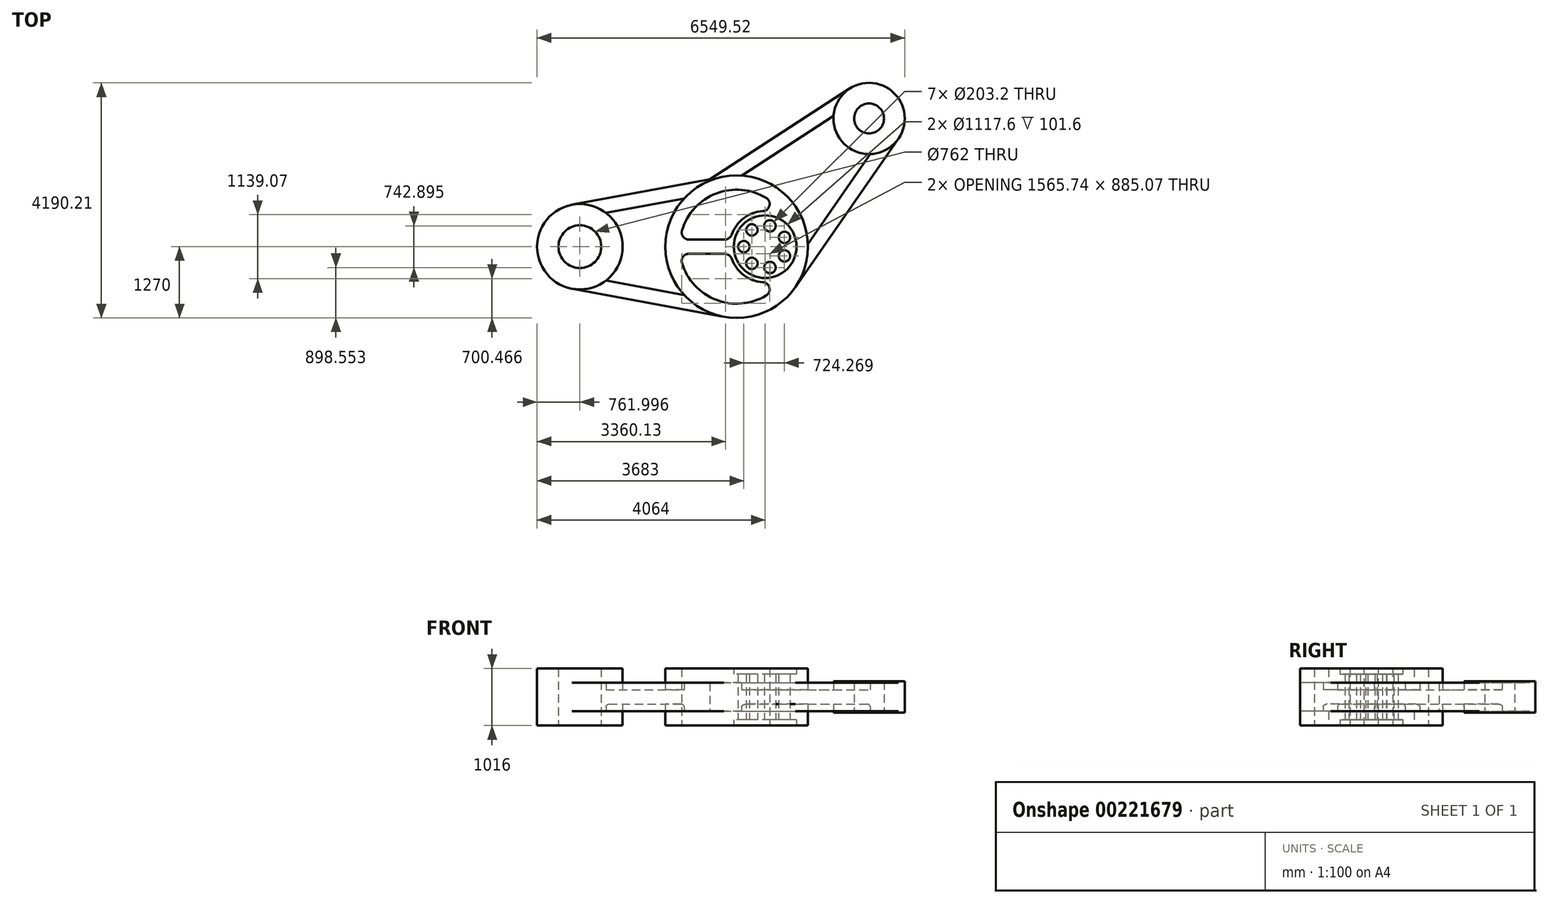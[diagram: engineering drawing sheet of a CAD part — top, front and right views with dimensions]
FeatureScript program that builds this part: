
annotation { "Feature Type Name" : "Feature", "Feature Type Description" : "" }
export const myFeature = defineFeature(function(context is Context, id is Id, definition is map)
    precondition{}
    {
        {
            var Q0;
            Q0=qCreatedBy(makeId("Top.planeOp"),FACE);
            var sketch = newSketch(context, id + "F0", { "sketchPlane" : qUnion([Q0])});
            skCircle(sketch, "E0", {"center": v(-3374.84, 0) * mm, "radius": 762 * mm});
            skCircle(sketch, "E1", {"center": v(-580.84, 0) * mm, "radius": 1270 * mm});
            skCircle(sketch, "E2", {"center": v(1777.68, 2285.21) * mm, "radius": 635 * mm});
            skCircle(sketch, "E3", {"center": v(-3374.84, 0) * mm, "radius": 381 * mm});
            skArc(sketch, "E4", {"start": v(-695.01, -127) * mm, "mid": v(-307.44, -590.07) * mm, "end": v(292.28, -519.53) * mm});
            skCircle(sketch, "E5", {"center": v(1777.68, 2285.21) * mm, "radius": 266.7 * mm});
            skArc(sketch, "E6", {"start": v(-1588.88, -127) * mm, "mid": v(-788.38, -994.58) * mm, "end": v(292.28, -519.53) * mm});
            skCircle(sketch, "E7", {"center": v(-72.84, 0) * mm, "radius": 558.8 * mm});
            skLineSegment(sketch, "E8", {"start": v(-3374.84, 0) * mm, "end": v(689.16, 0) * mm, "construction": true});
            skPoint(sketch, "E9.middle", {"position": v(-499.06, 0) * mm});
            skLineSegment(sketch, "E10", {"start": v(-3513.39, -749.3) * mm, "end": v(-811.75, -1248.83) * mm});
            skLineSegment(sketch, "E11", {"start": v(-3513.39, 749.3) * mm, "end": v(-1059.83, 1202.96) * mm});
            skLineSegment(sketch, "E12", {"start": v(462.58, -724) * mm, "end": v(2299.4, 1923.21) * mm});
            skLineSegment(sketch, "E13", {"start": v(-1059.83, 1202.96) * mm, "end": v(1432.34, 2818.1) * mm});
            skLineSegment(sketch, "E14.0", {"start": v(-2908.71, 602.8) * mm, "end": v(-1514.87, 860.52) * mm});
            skLineSegment(sketch, "E15.0", {"start": v(-2908.71, -602.8) * mm, "end": v(-1514.87, -860.52) * mm});
            skLineSegment(sketch, "E16.0", {"start": v(-493.95, 1267.02) * mm, "end": v(1144.17, 2328.66) * mm});
            skLineSegment(sketch, "E17.trimOffspring", {"start": v(688.3, 46.85) * mm, "end": v(1801.11, 1650.65) * mm});
            skLineSegment(sketch, "E18", {"start": v(-695.01, 127) * mm, "end": v(-1588.88, 127) * mm});
            skLineSegment(sketch, "E19.MirrorCS", {"start": v(-695.01, -127) * mm, "end": v(-1588.88, -127) * mm});
            skArc(sketch, "E20.trimOffspring", {"start": v(292.28, 519.53) * mm, "mid": v(-307.44, 590.07) * mm, "end": v(-695.01, 127) * mm});
            skArc(sketch, "E21.trimOffspring", {"start": v(292.28, 519.53) * mm, "mid": v(-788.38, 994.58) * mm, "end": v(-1588.88, 127) * mm});
            skPoint(sketch, "E22.center", {"position": v(0, 0) * mm});
            skLineSegment(sketch, "E23", {"start": v(-72.84, 0) * mm, "end": v(1777.68, 2285.21) * mm, "construction": true});
            skCircle(sketch, "E24", {"center": v(-453.84, 0) * mm, "radius": 101.6 * mm});
            skCircle(sketch, "E25.1.0", {"center": v(-310.4, -297.88) * mm, "radius": 101.6 * mm});
            skCircle(sketch, "E25.2.0", {"center": v(11.94, -371.45) * mm, "radius": 101.6 * mm});
            skCircle(sketch, "E25.3.0", {"center": v(270.42, -165.3) * mm, "radius": 101.6 * mm});
            skCircle(sketch, "E25.4.0", {"center": v(270.42, 165.3) * mm, "radius": 101.6 * mm});
            skCircle(sketch, "E25.5.0", {"center": v(11.94, 371.45) * mm, "radius": 101.6 * mm});
            skCircle(sketch, "E25.6.0", {"center": v(-310.4, 297.88) * mm, "radius": 101.6 * mm});
            skSolve(sketch);
        }
        {
            var Q0;
            Q0=makeQuery(id+"F0.imprint","IMPRINT",FACE,{"disambiguationData":[TD([[makeQuery(id+"F0.imprint","IMPRINT",EDGE,{"derivedFrom":sQuery(id+"F0.wireOp",EDGE,"E4")}),1.0]])]});
            extrude(context, id + "F1", {"entities" : qUnion([Q0]), "endBound" : BoundingType.SYMMETRIC, "depth" : 1016 * mm});
        }
        {
            var Q0;
            Q0=makeQuery(id+"F0.imprint","IMPRINT",FACE,{"disambiguationData":[TD([[makeQuery(id+"F0.imprint","IMPRINT",EDGE,{"derivedFrom":sQuery(id+"F0.wireOp",EDGE,"E7")}),1.0]])]});
            extrude(context, id + "F2", {"entities" : qUnion([Q0]), "operationType" : NewBodyOperationType.ADD, "endBound" : BoundingType.SYMMETRIC, "depth" : 812.8 * mm});
        }
        {
            var Q0;
            {var subQ3=sQuery(id+"F0.wireOp",EDGE,"E11");Q0=makeQuery(id+"F0.imprint","IMPRINT",FACE,{"disambiguationData":[TD([[makeQuery(id+"F0.imprint","IMPRINT",EDGE,{"derivedFrom":subQ3}),-1.0]])]});}
            extrude(context, id + "F3", {"entities" : qUnion([Q0]), "operationType" : NewBodyOperationType.ADD, "endBound" : BoundingType.SYMMETRIC, "depth" : 508 * mm});
        }
        {
            var Q0;
            {var subQ0=sQuery(id+"F0.wireOp",EDGE,"E10");Q0=makeQuery(id+"F0.imprint","IMPRINT",FACE,{"disambiguationData":[TD([[makeQuery(id+"F0.imprint","IMPRINT",EDGE,{"derivedFrom":subQ0}),1.0]])]});}
            var Q1;
            {var subQ0=sQuery(id+"F0.wireOp",EDGE,"E12");Q1=makeQuery(id+"F0.imprint","IMPRINT",FACE,{"disambiguationData":[TD([[makeQuery(id+"F0.imprint","IMPRINT",EDGE,{"derivedFrom":subQ0}),1.0]])]});}
            extrude(context, id + "F4", {"entities" : qUnion([Q0, Q1]), "operationType" : NewBodyOperationType.ADD, "endBound" : BoundingType.SYMMETRIC, "depth" : 508 * mm});
        }
        {
            var Q0;
            {var subQ0=sQuery(id+"F0.wireOp",EDGE,"E14.0");Q0=makeQuery(id+"F0.imprint","IMPRINT",FACE,{"disambiguationData":[TD([[makeQuery(id+"F0.imprint","IMPRINT",EDGE,{"derivedFrom":subQ0}),-1.0]])]});}
            var Q1;
            {var subQ0=sQuery(id+"F0.wireOp",EDGE,"E16.0");Q1=makeQuery(id+"F0.imprint","IMPRINT",FACE,{"disambiguationData":[TD([[makeQuery(id+"F0.imprint","IMPRINT",EDGE,{"derivedFrom":subQ0}),-1.0]])]});}
            extrude(context, id + "F5", {"entities" : qUnion([Q0, Q1]), "operationType" : NewBodyOperationType.ADD, "endBound" : BoundingType.SYMMETRIC, "depth" : 254 * mm});
        }
        {
            var Q0;
            Q0=makeQuery(id+"F0.imprint","IMPRINT",FACE,{"disambiguationData":[TD([[makeQuery(id+"F0.imprint","IMPRINT",EDGE,{"derivedFrom":sQuery(id+"F0.wireOp",EDGE,"E3")}),-1.0]])]});
            extrude(context, id + "F6", {"entities" : qUnion([Q0]), "operationType" : NewBodyOperationType.ADD, "endBound" : BoundingType.SYMMETRIC, "depth" : 1016 * mm});
        }
        {
            var Q0;
            Q0=makeQuery(id+"F0.imprint","IMPRINT",FACE,{"disambiguationData":[TD([[makeQuery(id+"F0.imprint","IMPRINT",EDGE,{"derivedFrom":sQuery(id+"F0.wireOp",EDGE,"E5")}),-1.0]])]});
            extrude(context, id + "F7", {"entities" : qUnion([Q0]), "operationType" : NewBodyOperationType.ADD, "endBound" : BoundingType.SYMMETRIC, "depth" : 558.8 * mm});
        }
        {
            var Q0;
            Q0=makeQuery(id+"F5.opExtrude","CAP_EDGE",EDGE,{"disambiguationData":[OSD([sQuery(id+"F0.wireOp",EDGE,"E16.0")])],"isStart":false});
            var Q1;
            Q1=makeQuery(id+"F5.opExtrude","CAP_EDGE",EDGE,{"disambiguationData":[OSD([sQuery(id+"F0.wireOp",EDGE,"E2")])],"isStart":false});
            var Q2;
            Q2=makeQuery(id+"F5.opExtrude","CAP_EDGE",EDGE,{"disambiguationData":[OSD([sQuery(id+"F0.wireOp",EDGE,"E17.trimOffspring")])],"isStart":false});
            var Q3;
            {var subQ0=sQuery(id+"F0.wireOp",EDGE,"E1");Q3=makeQuery(id+"F5.opExtrude","CAP_EDGE",EDGE,{"disambiguationData":[OSD([subQ0]),TDD([makeQuery(id+"F0.imprint","IMPRINT",EDGE,{"disambiguationData":[TD([[makeQuery(id+"F0.imprint","INTERSECT",VERTEX,{"derivedFrom":[subQ0,sQuery(id+"F0.wireOp",EDGE,"E16.0")]}),1.0]])],"derivedFrom":subQ0})])],"isStart":false});}
            var Q4;
            {var subQ0=sQuery(id+"F0.wireOp",EDGE,"E1");Q4=makeQuery(id+"F5.opExtrude","CAP_EDGE",EDGE,{"disambiguationData":[OSD([subQ0]),TDD([makeQuery(id+"F0.imprint","IMPRINT",EDGE,{"disambiguationData":[TD([[makeQuery(id+"F0.imprint","INTERSECT",VERTEX,{"derivedFrom":[subQ0,sQuery(id+"F0.wireOp",EDGE,"E14.0")]}),-1.0]])],"derivedFrom":subQ0})])],"isStart":false});}
            var Q5;
            Q5=makeQuery(id+"F5.opExtrude","CAP_EDGE",EDGE,{"disambiguationData":[OSD([sQuery(id+"F0.wireOp",EDGE,"E14.0")])],"isStart":false});
            var Q6;
            Q6=makeQuery(id+"F5.opExtrude","CAP_EDGE",EDGE,{"disambiguationData":[OSD([sQuery(id+"F0.wireOp",EDGE,"E15.0")])],"isStart":false});
            var Q7;
            Q7=makeQuery(id+"F5.opExtrude","CAP_EDGE",EDGE,{"disambiguationData":[OSD([sQuery(id+"F0.wireOp",EDGE,"E0")])],"isStart":false});
            var Q8;
            {var subQ0=sQuery(id+"F0.wireOp",EDGE,"E1");Q8=makeQuery(id+"F5.opExtrude","CAP_EDGE",EDGE,{"disambiguationData":[OSD([subQ0]),TDD([makeQuery(id+"F0.imprint","IMPRINT",EDGE,{"disambiguationData":[TD([[makeQuery(id+"F0.imprint","INTERSECT",VERTEX,{"derivedFrom":[subQ0,sQuery(id+"F0.wireOp",EDGE,"E16.0")]}),1.0]])],"derivedFrom":subQ0})])],"isStart":true});}
            var Q9;
            Q9=makeQuery(id+"F5.opExtrude","CAP_EDGE",EDGE,{"disambiguationData":[OSD([sQuery(id+"F0.wireOp",EDGE,"E16.0")])],"isStart":true});
            var Q10;
            Q10=makeQuery(id+"F5.opExtrude","CAP_EDGE",EDGE,{"disambiguationData":[OSD([sQuery(id+"F0.wireOp",EDGE,"E2")])],"isStart":true});
            var Q11;
            Q11=makeQuery(id+"F5.opExtrude","CAP_EDGE",EDGE,{"disambiguationData":[OSD([sQuery(id+"F0.wireOp",EDGE,"E17.trimOffspring")])],"isStart":true});
            var Q12;
            {var subQ0=sQuery(id+"F0.wireOp",EDGE,"E1");Q12=makeQuery(id+"F5.opExtrude","CAP_EDGE",EDGE,{"disambiguationData":[OSD([subQ0]),TDD([makeQuery(id+"F0.imprint","IMPRINT",EDGE,{"disambiguationData":[TD([[makeQuery(id+"F0.imprint","INTERSECT",VERTEX,{"derivedFrom":[subQ0,sQuery(id+"F0.wireOp",EDGE,"E14.0")]}),-1.0]])],"derivedFrom":subQ0})])],"isStart":true});}
            var Q13;
            Q13=makeQuery(id+"F5.opExtrude","CAP_EDGE",EDGE,{"disambiguationData":[OSD([sQuery(id+"F0.wireOp",EDGE,"E14.0")])],"isStart":true});
            var Q14;
            Q14=makeQuery(id+"F5.opExtrude","CAP_EDGE",EDGE,{"disambiguationData":[OSD([sQuery(id+"F0.wireOp",EDGE,"E15.0")])],"isStart":true});
            var Q15;
            Q15=makeQuery(id+"F5.opExtrude","CAP_EDGE",EDGE,{"disambiguationData":[OSD([sQuery(id+"F0.wireOp",EDGE,"E0")])],"isStart":true});
            fillet(context, id + "F8", {"entities" : qUnion([Q0, Q1, Q2, Q3, Q4, Q5, Q6, Q7, Q8, Q9, Q10, Q11, Q12, Q13, Q14, Q15]), "radius" : 50.8 * mm, "tangentPropagation" : true, "allowEdgeOverflow" : false});
        }
        {
            var Q0;
            {var subQ0=sQuery(id+"F0.wireOp",EDGE,"E2");var subQ1=sQuery(id+"F0.wireOp",EDGE,"E16.0");var subQ2=sQuery(id+"F0.wireOp",EDGE,"E1");Q0=makeQuery(id+"F5.boolean.opBoolean","SPLIT",EDGE,{"disambiguationData":[TD([makeQuery(id+"F5.opExtrude","CAP_FACE",FACE,{"disambiguationData":[OSD([subQ2,subQ0,subQ1,sQuery(id+"F0.wireOp",EDGE,"E17.trimOffspring")])],"isStart":false})])],"derivedFrom":makeQuery(id+"F3.opExtrude","SWEPT_EDGE",EDGE,{"disambiguationData":[OSD([subQ0,subQ1])]})});}
            var Q1;
            {var subQ0=sQuery(id+"F0.wireOp",EDGE,"E1");var subQ1=sQuery(id+"F0.wireOp",EDGE,"E14.0");var subQ2=sQuery(id+"F0.wireOp",EDGE,"E0");Q1=makeQuery(id+"F5.boolean.opBoolean","SPLIT",EDGE,{"disambiguationData":[TD([makeQuery(id+"F5.opExtrude","CAP_FACE",FACE,{"disambiguationData":[OSD([subQ2,subQ0,subQ1,sQuery(id+"F0.wireOp",EDGE,"E15.0")])],"isStart":false})])],"derivedFrom":makeQuery(id+"F3.opExtrude","SWEPT_EDGE",EDGE,{"disambiguationData":[OSD([subQ0,subQ1])]})});}
            var Q2;
            {var subQ0=sQuery(id+"F0.wireOp",EDGE,"E1");var subQ1=sQuery(id+"F0.wireOp",EDGE,"E15.0");var subQ2=sQuery(id+"F0.wireOp",EDGE,"E0");Q2=makeQuery(id+"F5.boolean.opBoolean","SPLIT",EDGE,{"disambiguationData":[TD([makeQuery(id+"F4.opExtrude","CAP_FACE",FACE,{"disambiguationData":[OSD([subQ2,subQ0,sQuery(id+"F0.wireOp",EDGE,"E10"),subQ1])],"isStart":false})])],"derivedFrom":makeQuery(id+"F4.opExtrude","SWEPT_EDGE",EDGE,{"disambiguationData":[OSD([subQ0,subQ1])]})});}
            var Q3;
            {var subQ0=sQuery(id+"F0.wireOp",EDGE,"E15.0");var subQ1=sQuery(id+"F0.wireOp",EDGE,"E1");var subQ2=sQuery(id+"F0.wireOp",EDGE,"E0");Q3=makeQuery(id+"F5.boolean.opBoolean","SPLIT",EDGE,{"disambiguationData":[TD([makeQuery(id+"F4.opExtrude","CAP_FACE",FACE,{"disambiguationData":[OSD([subQ2,subQ1,sQuery(id+"F0.wireOp",EDGE,"E10"),subQ0])],"isStart":false})])],"derivedFrom":makeQuery(id+"F4.opExtrude","SWEPT_EDGE",EDGE,{"disambiguationData":[OSD([subQ2,subQ0])]})});}
            var Q4;
            {var subQ0=sQuery(id+"F0.wireOp",EDGE,"E14.0");var subQ1=sQuery(id+"F0.wireOp",EDGE,"E0");var subQ2=sQuery(id+"F0.wireOp",EDGE,"E1");Q4=makeQuery(id+"F5.boolean.opBoolean","SPLIT",EDGE,{"disambiguationData":[TD([makeQuery(id+"F5.opExtrude","CAP_FACE",FACE,{"disambiguationData":[OSD([subQ1,subQ2,subQ0,sQuery(id+"F0.wireOp",EDGE,"E15.0")])],"isStart":false})])],"derivedFrom":makeQuery(id+"F3.opExtrude","SWEPT_EDGE",EDGE,{"disambiguationData":[OSD([subQ1,subQ0])]})});}
            var Q5;
            Q5=makeQuery(id+"F1.opExtrude","SWEPT_EDGE",EDGE,{"disambiguationData":[OSD([sQuery(id+"F0.wireOp",EDGE,"E18"),sQuery(id+"F0.wireOp",EDGE,"E21.trimOffspring")])]});
            var Q6;
            Q6=makeQuery(id+"F1.opExtrude","SWEPT_EDGE",EDGE,{"disambiguationData":[OSD([sQuery(id+"F0.wireOp",EDGE,"E18"),sQuery(id+"F0.wireOp",EDGE,"E20.trimOffspring")])]});
            var Q7;
            Q7=makeQuery(id+"F1.opExtrude","SWEPT_EDGE",EDGE,{"disambiguationData":[OSD([sQuery(id+"F0.wireOp",EDGE,"E20.trimOffspring"),sQuery(id+"F0.wireOp",EDGE,"E21.trimOffspring")])]});
            var Q8;
            Q8=makeQuery(id+"F1.opExtrude","SWEPT_EDGE",EDGE,{"disambiguationData":[OSD([sQuery(id+"F0.wireOp",EDGE,"E4"),sQuery(id+"F0.wireOp",EDGE,"E19.MirrorCS")])]});
            var Q9;
            Q9=makeQuery(id+"F1.opExtrude","SWEPT_EDGE",EDGE,{"disambiguationData":[OSD([sQuery(id+"F0.wireOp",EDGE,"E6"),sQuery(id+"F0.wireOp",EDGE,"E19.MirrorCS")])]});
            var Q10;
            Q10=makeQuery(id+"F1.opExtrude","SWEPT_EDGE",EDGE,{"disambiguationData":[OSD([sQuery(id+"F0.wireOp",EDGE,"E4"),sQuery(id+"F0.wireOp",EDGE,"E6")])]});
            var Q11;
            {var subQ0=sQuery(id+"F0.wireOp",EDGE,"E1");var subQ1=sQuery(id+"F0.wireOp",EDGE,"E17.trimOffspring");var subQ2=sQuery(id+"F0.wireOp",EDGE,"E2");Q11=makeQuery(id+"F5.boolean.opBoolean","SPLIT",EDGE,{"disambiguationData":[TD([makeQuery(id+"F4.opExtrude","CAP_FACE",FACE,{"disambiguationData":[OSD([subQ0,subQ2,sQuery(id+"F0.wireOp",EDGE,"E12"),subQ1])],"isStart":false})])],"derivedFrom":makeQuery(id+"F4.opExtrude","SWEPT_EDGE",EDGE,{"disambiguationData":[OSD([subQ0,subQ1])]})});}
            var Q12;
            {var subQ0=sQuery(id+"F0.wireOp",EDGE,"E1");var subQ1=sQuery(id+"F0.wireOp",EDGE,"E16.0");var subQ2=sQuery(id+"F0.wireOp",EDGE,"E2");Q12=makeQuery(id+"F5.boolean.opBoolean","SPLIT",EDGE,{"disambiguationData":[TD([makeQuery(id+"F5.opExtrude","CAP_FACE",FACE,{"disambiguationData":[OSD([subQ0,subQ2,subQ1,sQuery(id+"F0.wireOp",EDGE,"E17.trimOffspring")])],"isStart":false})])],"derivedFrom":makeQuery(id+"F3.opExtrude","SWEPT_EDGE",EDGE,{"disambiguationData":[OSD([subQ0,subQ1])]})});}
            var Q13;
            {var subQ0=sQuery(id+"F0.wireOp",EDGE,"E17.trimOffspring");var subQ1=sQuery(id+"F0.wireOp",EDGE,"E2");var subQ2=sQuery(id+"F0.wireOp",EDGE,"E1");Q13=makeQuery(id+"F5.boolean.opBoolean","SPLIT",EDGE,{"disambiguationData":[TD([makeQuery(id+"F4.opExtrude","CAP_FACE",FACE,{"disambiguationData":[OSD([subQ2,subQ1,sQuery(id+"F0.wireOp",EDGE,"E12"),subQ0])],"isStart":false})])],"derivedFrom":makeQuery(id+"F4.opExtrude","SWEPT_EDGE",EDGE,{"disambiguationData":[OSD([subQ1,subQ0])]})});}
            var Q14;
            {var subQ0=sQuery(id+"F0.wireOp",EDGE,"E1");var subQ1=sQuery(id+"F0.wireOp",EDGE,"E16.0");var subQ2=sQuery(id+"F0.wireOp",EDGE,"E2");Q14=makeQuery(id+"F5.boolean.opBoolean","SPLIT",EDGE,{"disambiguationData":[TD([makeQuery(id+"F5.opExtrude","CAP_FACE",FACE,{"disambiguationData":[OSD([subQ0,subQ2,subQ1,sQuery(id+"F0.wireOp",EDGE,"E17.trimOffspring")])],"isStart":true})])],"derivedFrom":makeQuery(id+"F3.opExtrude","SWEPT_EDGE",EDGE,{"disambiguationData":[OSD([subQ0,subQ1])]})});}
            var Q15;
            {var subQ0=sQuery(id+"F0.wireOp",EDGE,"E1");var subQ1=sQuery(id+"F0.wireOp",EDGE,"E17.trimOffspring");var subQ2=sQuery(id+"F0.wireOp",EDGE,"E2");Q15=makeQuery(id+"F5.boolean.opBoolean","SPLIT",EDGE,{"disambiguationData":[TD([makeQuery(id+"F4.opExtrude","CAP_FACE",FACE,{"disambiguationData":[OSD([subQ0,subQ2,sQuery(id+"F0.wireOp",EDGE,"E12"),subQ1])],"isStart":true})])],"derivedFrom":makeQuery(id+"F4.opExtrude","SWEPT_EDGE",EDGE,{"disambiguationData":[OSD([subQ0,subQ1])]})});}
            var Q16;
            {var subQ0=sQuery(id+"F0.wireOp",EDGE,"E17.trimOffspring");var subQ1=sQuery(id+"F0.wireOp",EDGE,"E2");var subQ2=sQuery(id+"F0.wireOp",EDGE,"E1");Q16=makeQuery(id+"F5.boolean.opBoolean","SPLIT",EDGE,{"disambiguationData":[TD([makeQuery(id+"F4.opExtrude","CAP_FACE",FACE,{"disambiguationData":[OSD([subQ2,subQ1,sQuery(id+"F0.wireOp",EDGE,"E12"),subQ0])],"isStart":true})])],"derivedFrom":makeQuery(id+"F4.opExtrude","SWEPT_EDGE",EDGE,{"disambiguationData":[OSD([subQ1,subQ0])]})});}
            var Q17;
            {var subQ0=sQuery(id+"F0.wireOp",EDGE,"E2");var subQ1=sQuery(id+"F0.wireOp",EDGE,"E16.0");var subQ2=sQuery(id+"F0.wireOp",EDGE,"E1");Q17=makeQuery(id+"F5.boolean.opBoolean","SPLIT",EDGE,{"disambiguationData":[TD([makeQuery(id+"F5.opExtrude","CAP_FACE",FACE,{"disambiguationData":[OSD([subQ2,subQ0,subQ1,sQuery(id+"F0.wireOp",EDGE,"E17.trimOffspring")])],"isStart":true})])],"derivedFrom":makeQuery(id+"F3.opExtrude","SWEPT_EDGE",EDGE,{"disambiguationData":[OSD([subQ0,subQ1])]})});}
            var Q18;
            {var subQ0=sQuery(id+"F0.wireOp",EDGE,"E1");var subQ1=sQuery(id+"F0.wireOp",EDGE,"E15.0");var subQ2=sQuery(id+"F0.wireOp",EDGE,"E0");Q18=makeQuery(id+"F5.boolean.opBoolean","SPLIT",EDGE,{"disambiguationData":[TD([makeQuery(id+"F4.opExtrude","CAP_FACE",FACE,{"disambiguationData":[OSD([subQ2,subQ0,sQuery(id+"F0.wireOp",EDGE,"E10"),subQ1])],"isStart":true})])],"derivedFrom":makeQuery(id+"F4.opExtrude","SWEPT_EDGE",EDGE,{"disambiguationData":[OSD([subQ0,subQ1])]})});}
            var Q19;
            {var subQ0=sQuery(id+"F0.wireOp",EDGE,"E1");var subQ1=sQuery(id+"F0.wireOp",EDGE,"E14.0");var subQ2=sQuery(id+"F0.wireOp",EDGE,"E0");Q19=makeQuery(id+"F5.boolean.opBoolean","SPLIT",EDGE,{"disambiguationData":[TD([makeQuery(id+"F5.opExtrude","CAP_FACE",FACE,{"disambiguationData":[OSD([subQ2,subQ0,subQ1,sQuery(id+"F0.wireOp",EDGE,"E15.0")])],"isStart":true})])],"derivedFrom":makeQuery(id+"F3.opExtrude","SWEPT_EDGE",EDGE,{"disambiguationData":[OSD([subQ0,subQ1])]})});}
            var Q20;
            {var subQ0=sQuery(id+"F0.wireOp",EDGE,"E15.0");var subQ1=sQuery(id+"F0.wireOp",EDGE,"E1");var subQ2=sQuery(id+"F0.wireOp",EDGE,"E0");Q20=makeQuery(id+"F5.boolean.opBoolean","SPLIT",EDGE,{"disambiguationData":[TD([makeQuery(id+"F4.opExtrude","CAP_FACE",FACE,{"disambiguationData":[OSD([subQ2,subQ1,sQuery(id+"F0.wireOp",EDGE,"E10"),subQ0])],"isStart":true})])],"derivedFrom":makeQuery(id+"F4.opExtrude","SWEPT_EDGE",EDGE,{"disambiguationData":[OSD([subQ2,subQ0])]})});}
            var Q21;
            {var subQ0=sQuery(id+"F0.wireOp",EDGE,"E14.0");var subQ1=sQuery(id+"F0.wireOp",EDGE,"E0");var subQ2=sQuery(id+"F0.wireOp",EDGE,"E1");Q21=makeQuery(id+"F5.boolean.opBoolean","SPLIT",EDGE,{"disambiguationData":[TD([makeQuery(id+"F5.opExtrude","CAP_FACE",FACE,{"disambiguationData":[OSD([subQ1,subQ2,subQ0,sQuery(id+"F0.wireOp",EDGE,"E15.0")])],"isStart":true})])],"derivedFrom":makeQuery(id+"F3.opExtrude","SWEPT_EDGE",EDGE,{"disambiguationData":[OSD([subQ1,subQ0])]})});}
            fillet(context, id + "F9", {"entities" : qUnion([Q0, Q1, Q2, Q3, Q4, Q5, Q6, Q7, Q8, Q9, Q10, Q11, Q12, Q13, Q14, Q15, Q16, Q17, Q18, Q19, Q20, Q21]), "radius" : 127 * mm, "tangentPropagation" : true, "allowEdgeOverflow" : false});
        }
    });
